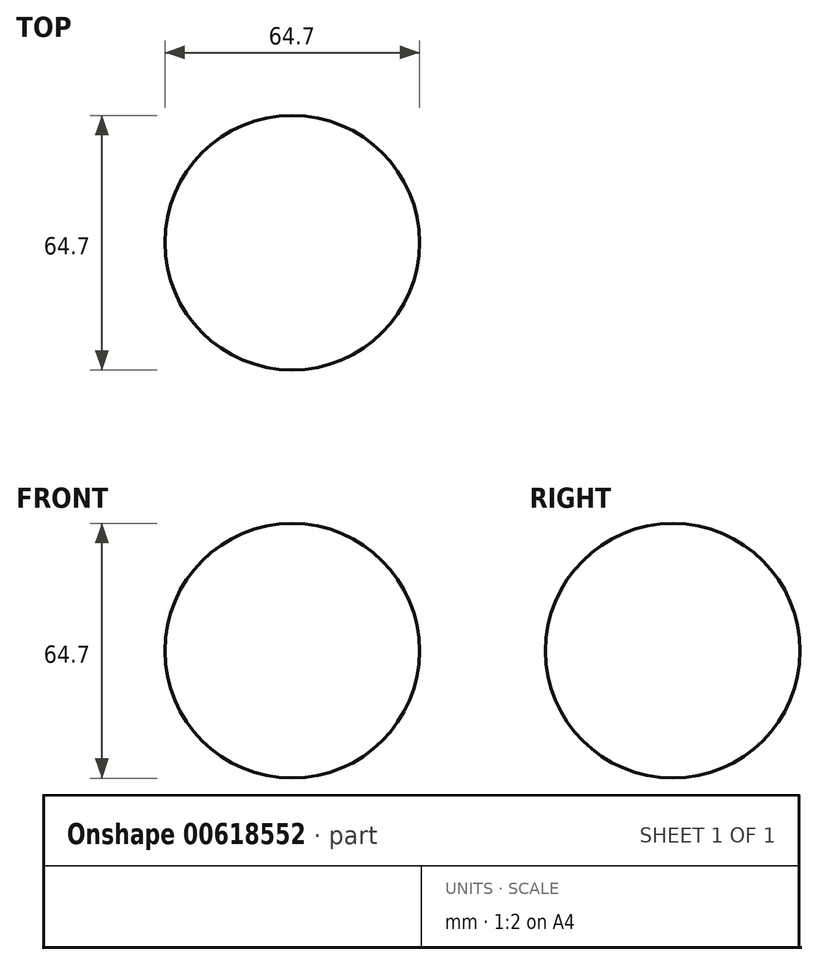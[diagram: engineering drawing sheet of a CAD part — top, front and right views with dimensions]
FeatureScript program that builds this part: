
annotation { "Feature Type Name" : "Feature", "Feature Type Description" : "" }
export const myFeature = defineFeature(function(context is Context, id is Id, definition is map)
    precondition{}
    {
        {
            var Q0;
            Q0=qCreatedBy(makeId("Front.planeOp"),FACE);
            var sketch = newSketch(context, id + "F0", { "sketchPlane" : qUnion([Q0])});
            skLineSegment(sketch, "E0", {"start": v(0, 70.04) * mm, "end": v(0, -66.24) * mm, "construction": true});
            skSolve(sketch);
        }
        {
            var Q0;
            Q0=qCreatedBy(makeId("Front.planeOp"),FACE);
            var sketch = newSketch(context, id + "F1", { "sketchPlane" : qUnion([Q0])});
            skArc(sketch, "E1", {"start": v(0, 31) * mm, "mid": v(-32.35, -1.36) * mm, "end": v(0, -33.7) * mm});
            skLineSegment(sketch, "E2", {"start": v(0, 31) * mm, "end": v(0, -33.7) * mm});
            skSolve(sketch);
        }
        {
            var Q0;
            Q0 = qSketchRegion(id + "F1", true);
            var Q1;
            Q1=sQuery(id+"F0.wireOp",EDGE,"E0");
            revolve(context, id + "F2", {"entities" : qUnion([Q0]), "axis" : qUnion([Q1]), "revolveType" : RevolveType.FULL});
        }
    });
